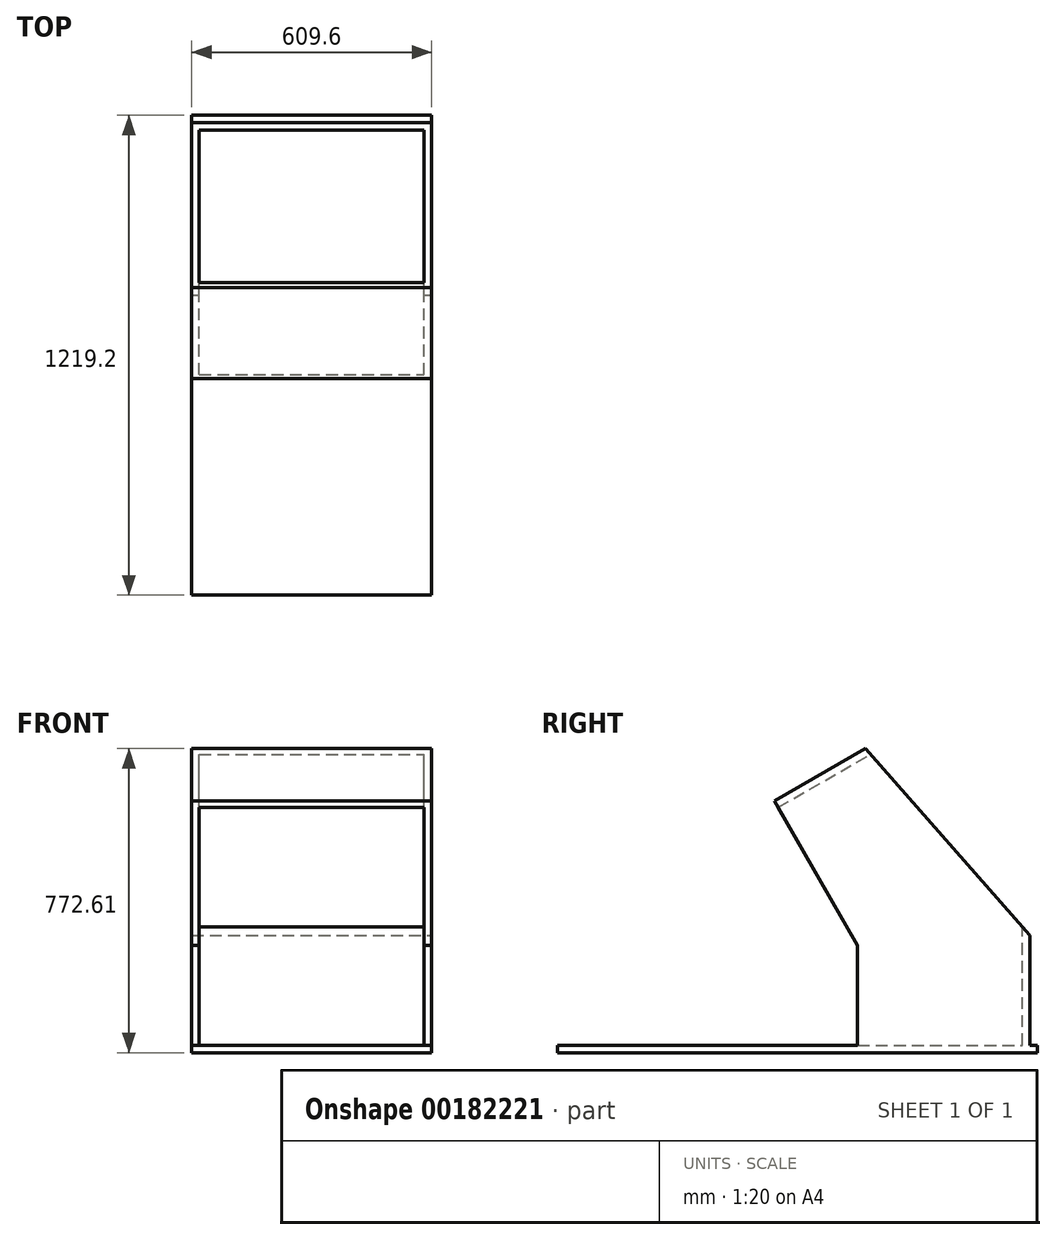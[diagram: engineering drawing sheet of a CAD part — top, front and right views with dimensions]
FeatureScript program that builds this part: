
annotation { "Feature Type Name" : "Feature", "Feature Type Description" : "" }
export const myFeature = defineFeature(function(context is Context, id is Id, definition is map)
    precondition{}
    {
        {
            var Q0;
            Q0=qCreatedBy(makeId("Right.planeOp"),FACE);
            var sketch = newSketch(context, id + "F0", { "sketchPlane" : qUnion([Q0])});
            skLineSegment(sketch, "E0.bottom", {"start": v(0, 0) * mm, "end": v(1219.2, 0) * mm});
            skLineSegment(sketch, "E0.top", {"start": v(0, 19.05) * mm, "end": v(1219.2, 19.05) * mm});
            skLineSegment(sketch, "E0.left", {"start": v(0, 0) * mm, "end": v(0, 19.05) * mm});
            skLineSegment(sketch, "E0.right", {"start": v(1219.2, 0) * mm, "end": v(1219.2, 19.05) * mm});
            skSolve(sketch);
        }
        {
            var Q0;
            Q0=qCreatedBy(makeId("Right.planeOp"),FACE);
            var sketch = newSketch(context, id + "F1", { "sketchPlane" : qUnion([Q0])});
            skLineSegment(sketch, "E1.left", {"start": v(1200.15, 19.05) * mm, "end": v(1200.15, 298.45) * mm});
            skLineSegment(sketch, "E2", {"start": v(1200.15, 298.45) * mm, "end": v(781.54, 772.6) * mm});
            skLineSegment(sketch, "E3", {"start": v(550.57, 639.26) * mm, "end": v(762, 273.05) * mm});
            skLineSegment(sketch, "E4", {"start": v(762, 273.05) * mm, "end": v(762, 19.05) * mm});
            skLineSegment(sketch, "E5", {"start": v(550.57, 639.26) * mm, "end": v(781.54, 772.6) * mm});
            skLineSegment(sketch, "E6", {"start": v(762, 19.05) * mm, "end": v(1200.15, 19.05) * mm});
            skSolve(sketch);
        }
        {
            var Q0;
            Q0=qSketchRegion(id+"F0",true);
            extrude(context, id + "F2", {"entities" : qUnion([Q0]), "oppositeDirection" : true, "depth" : 609.6 * mm});
        }
        {
            var Q0;
            Q0=qSketchRegion(id+"F1",true);
            extrude(context, id + "F3", {"entities" : qUnion([Q0]), "operationType" : NewBodyOperationType.ADD, "oppositeDirection" : true, "depth" : 609.6 * mm});
        }
        {
            var Q0;
            Q0=makeQuery(id+"F3.opExtrude","SWEPT_FACE",FACE,{"disambiguationData":[OSD([sQuery(id+"F1.wireOp",EDGE,"E3")])]});
            var Q1;
            Q1=makeQuery(id+"F3.opExtrude","SWEPT_FACE",FACE,{"disambiguationData":[OSD([sQuery(id+"F1.wireOp",EDGE,"E4")])]});
            var Q2;
            Q2=makeQuery(id+"F3.opExtrude","SWEPT_FACE",FACE,{"disambiguationData":[OSD([sQuery(id+"F1.wireOp",EDGE,"E2")])]});
            shell(context, id + "F4", {"entities" : qUnion([Q0, Q1, Q2]), "thickness" : 19.05 * mm});
        }
    });
